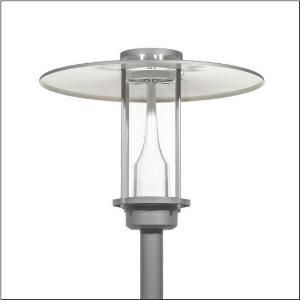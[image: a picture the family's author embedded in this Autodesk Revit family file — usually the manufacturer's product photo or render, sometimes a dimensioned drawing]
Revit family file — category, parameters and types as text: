
# Revit family: city-light_plus_iq___p1_0a_5xa5275nf14hp_e05b
name_source: partatom
category: Lighting Fixtures
units: mm (PartAtom-declared; Revit-internal decimal feet)

## family parameters
Cut with Voids When Loaded = No
Host = Face
Light Source = No
Part Type = Normal
Room Calculation Point = No
Round Connector Dimension = Use Diameter
Shared = No

## types (1)
- --- (1 x LED, 4020 lm, 33.6 W, 2700K)
    Apparent Load = 34 VA
    CIE Flux Codes = 30 60 90 96 100
    Color Rendering = 70
    Color Temperature = 2700K
    Default Elevation = 1800 mm
    Description = City-Light Plus iQ, mast luminaire, Module 540 iQ-SR, primary light control with 3 zone facetted reflector, of plastic, silver coated, highly specular, structured, primary optical cover: cover, of PMMA, transparent, light distribution: P1.0a, light emission: direct distribution, primary light characteristic: strongly asymmetric, installation type: post-top, LED, High Power LED, rated luminous flux: 4.020lm, luminous efficacy: 120lm/W, light colour: 727, colour temperature: 2700K, control gear: ECG iQ, control: pre-setting: logarithmic dimming characteristic, Street-Remote, Auto-Match, Temp-Guard, Lumen-Switch, Night-Set, Smart-Wire, Light-Fading, Desk-Remote (wireless, voltage-free reading and setting of iQ features in the workshop via application-optimized NFC function/RFID function), optimised constant luminous flux control (CLO 2.0), with terminal, 6-pole, max. 2.5mm², mains connection: 230..240V, AC, 50/60Hz, start of lifetime: 34W, end of service life: 36W, reduction: 15W, luminaire housing, upper part, of glass-fibre reinforced polyester, coated, Siteco® metallic grey (DB 702S), diameter: 750mm, height: 590mm, spigot size: d x l = 76 x 70mm (post-top) | with reducer (optional accessory) 60 x 70mm, post-top mast mounting element, of diecast aluminium, coated, Siteco® metallic grey (DB 702S), Module 540 iQ-SR, traffic white (RAL 9016), equipment: Power, protection rating (complete): IP65, insulation class (complete): insulation class II (safety insulation), certification: CE, ENEC, VDE, packaging unit: 1 piece

Light Distribution: P1.0a
    Height = 590 mm
    Lamp = 1 x LED
    Lamp Light Flux = 4020 lm
    Lamp Power = 33.6 W
    Lamp count = 1
    Length = 750 mm
    Luminous efficacy = 120 lm/W
    Manufacturer = Siteco
    ModVariant = No
    Model = 5XA5275NF14HP
    Number of Poles = 1
    OnlyDefault = Yes
    Power Factor = 1
    Product Name = City-Light Plus iQ | P1.0a
    Product group = mast luminaire | pylon top
    ProductGroupID = 6100
    Protection Class = Protection class II
    Protection Degree = IP 65
    RLX_Detail_Level = 1
    RLX_Emergency_Light_Flux = 0 lm
    RLX_Emergency_Type = 0
    RLX_Emergency_Type_DB = No
    RlxData = <blob elided: 52469 chars, md5=a86d5f59>
    Socket = socket
    Standby Power = 0 W
    System Light Flux = 4020 lm
    System Power = 34 W
    Type Comments = factory setting: luminous flux: 100 % | dim-lin: 254 | 695 mA
    Type Image = l_1006456.jpg
    URL = http://relux.com
    VarID = @adj_123179
    Voltage = 0 V
    Weight = 0.00 kg
    Width = 0 mm  [stored 0 ft]

note: [stored X ft] marks values corroborated as IEEE doubles in the binary element streams (Revit-internal decimal feet)

## geometry (parser evidence)
native form markers: Blend x4, Sweep x11
no freeform markers — native parametric forms only
